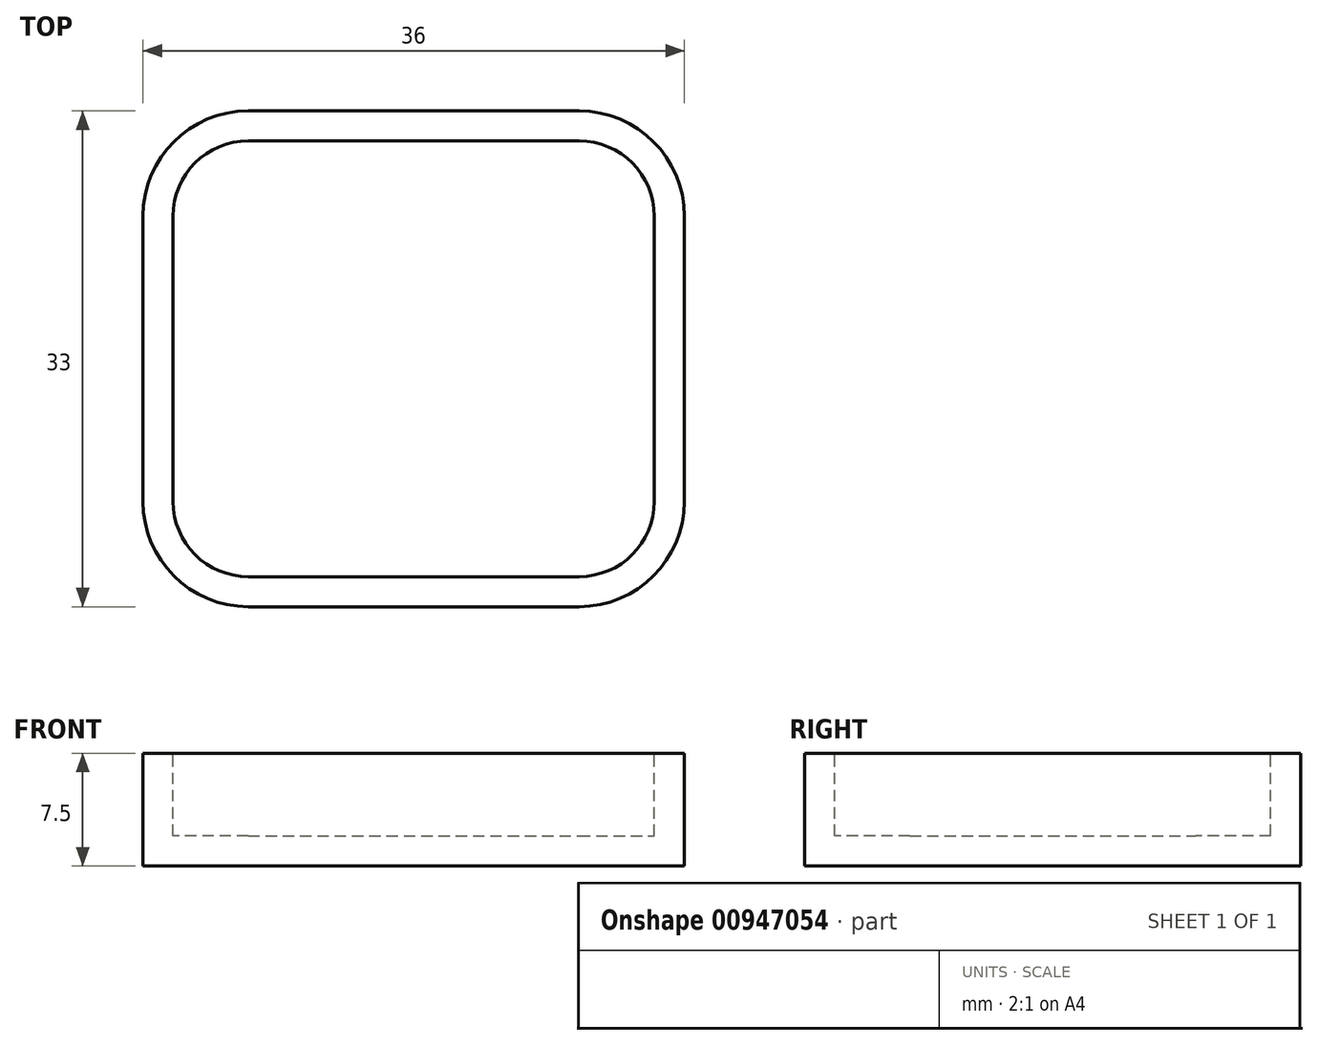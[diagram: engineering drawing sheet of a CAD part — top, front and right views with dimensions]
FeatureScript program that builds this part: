
annotation { "Feature Type Name" : "Feature", "Feature Type Description" : "" }
export const myFeature = defineFeature(function(context is Context, id is Id, definition is map)
    precondition{}
    {
        {
            var Q0;
            Q0=qCreatedBy(makeId("Top.planeOp"),FACE);
            var sketch = newSketch(context, id + "F0", { "sketchPlane" : qUnion([Q0])});
            skLineSegment(sketch, "E0.bottom", {"start": v(5, 0) * mm, "end": v(27, 0) * mm});
            skLineSegment(sketch, "E0.top", {"start": v(5, 29) * mm, "end": v(27, 29) * mm});
            skLineSegment(sketch, "E0.left", {"start": v(0, 5) * mm, "end": v(0, 24) * mm});
            skLineSegment(sketch, "E0.right", {"start": v(32, 5) * mm, "end": v(32, 24) * mm});
            skPoint(sketch, "E1.visualSharp", {"position": v(0, 29) * mm});
            skArc(sketch, "E1.filletArc", {"start": v(5, 29) * mm, "mid": v(1.46, 27.54) * mm, "end": v(0, 24) * mm});
            skPoint(sketch, "E2.visualSharp", {"position": v(0, 0) * mm});
            skArc(sketch, "E2.filletArc", {"start": v(0, 5) * mm, "mid": v(1.46, 1.46) * mm, "end": v(5, 0) * mm});
            skPoint(sketch, "E3.visualSharp", {"position": v(32, 0) * mm});
            skArc(sketch, "E3.filletArc", {"start": v(27, 0) * mm, "mid": v(30.54, 1.46) * mm, "end": v(32, 5) * mm});
            skPoint(sketch, "E4.visualSharp", {"position": v(32, 29) * mm});
            skArc(sketch, "E4.filletArc", {"start": v(32, 24) * mm, "mid": v(30.54, 27.54) * mm, "end": v(27, 29) * mm});
            skArc(sketch, "E5.0", {"start": v(5, 31) * mm, "mid": v(0.05, 28.95) * mm, "end": v(-2, 24) * mm});
            skLineSegment(sketch, "E5.1", {"start": v(-2, 5) * mm, "end": v(-2, 24) * mm});
            skLineSegment(sketch, "E5.2", {"start": v(5, 31) * mm, "end": v(27, 31) * mm});
            skArc(sketch, "E5.3", {"start": v(-2, 5) * mm, "mid": v(0.05, 0.05) * mm, "end": v(5, -2) * mm});
            skArc(sketch, "E5.4", {"start": v(34, 24) * mm, "mid": v(31.95, 28.95) * mm, "end": v(27, 31) * mm});
            skLineSegment(sketch, "E5.5", {"start": v(34, 5) * mm, "end": v(34, 24) * mm});
            skArc(sketch, "E5.6", {"start": v(27, -2) * mm, "mid": v(31.95, 0.05) * mm, "end": v(34, 5) * mm});
            skLineSegment(sketch, "E5.7", {"start": v(5, -2) * mm, "end": v(27, -2) * mm});
            skSolve(sketch);
        }
        {
            var Q0;
            Q0 = qSketchRegion(id + "F0", true);
            var Q1;
            Q1=makeQuery(id+"F0.imprint","IMPRINT",FACE,{"disambiguationData":[TD([[makeQuery(id+"F0.imprint","IMPRINT",EDGE,{"derivedFrom":sQuery(id+"F0.wireOp",EDGE,"E0.bottom")}),1.0]])]});
            extrude(context, id + "F1", {"entities" : qUnion([Q0, Q1]), "depth" : 7.5 * mm, "offsetDistance" : 25 * mm});
        }
        {
            var Q0;
            Q0=makeQuery(id+"F1.opExtrude","CAP_FACE",FACE,{"disambiguationData":[OSD([sQuery(id+"F0.wireOp",EDGE,"E5.0"),sQuery(id+"F0.wireOp",EDGE,"E5.1"),sQuery(id+"F0.wireOp",EDGE,"E5.2"),sQuery(id+"F0.wireOp",EDGE,"E5.3"),sQuery(id+"F0.wireOp",EDGE,"E5.4"),sQuery(id+"F0.wireOp",EDGE,"E5.5"),sQuery(id+"F0.wireOp",EDGE,"E5.6"),sQuery(id+"F0.wireOp",EDGE,"E5.7")])],"isStart":false});
            shell(context, id + "F2", {"entities" : qUnion([Q0]), "thickness" : 2 * mm});
        }
    });
